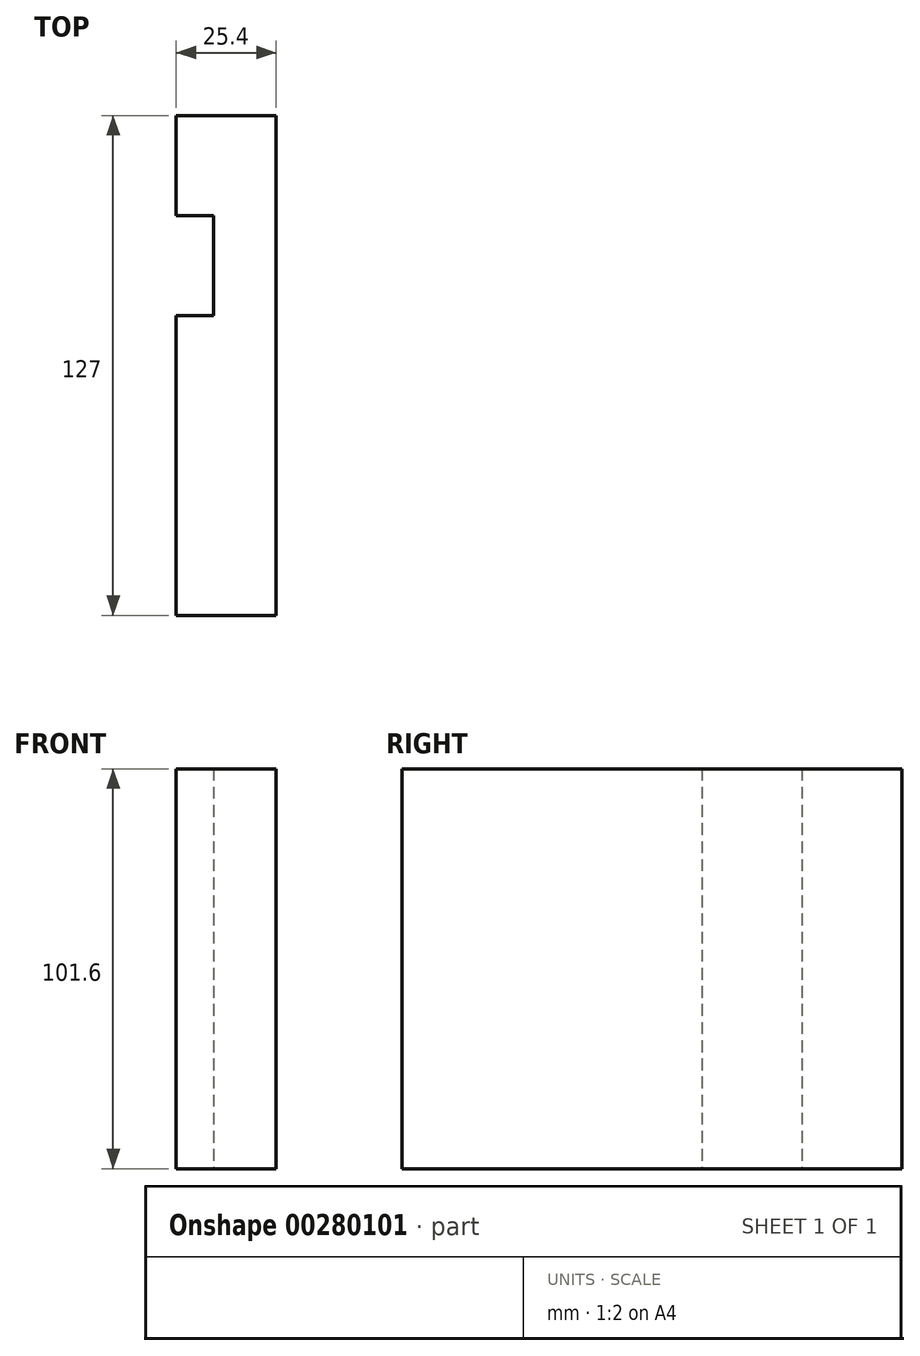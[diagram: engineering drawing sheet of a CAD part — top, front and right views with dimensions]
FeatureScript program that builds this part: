
annotation { "Feature Type Name" : "Feature", "Feature Type Description" : "" }
export const myFeature = defineFeature(function(context is Context, id is Id, definition is map)
    precondition{}
    {
        {
            var Q0;
            Q0=qCreatedBy(makeId("Top.planeOp"),FACE);
            var sketch = newSketch(context, id + "F0", { "sketchPlane" : qUnion([Q0])});
            skLineSegment(sketch, "E0", {"start": v(-9.74, 0) * mm, "end": v(-9.74, 127) * mm});
            skLineSegment(sketch, "E1", {"start": v(-9.74, 127) * mm, "end": v(-35.14, 127) * mm});
            skLineSegment(sketch, "E2", {"start": v(-35.14, 127) * mm, "end": v(-35.14, 101.6) * mm});
            skLineSegment(sketch, "E3", {"start": v(-35.14, 101.6) * mm, "end": v(-25.61, 101.6) * mm});
            skLineSegment(sketch, "E4", {"start": v(-25.61, 101.6) * mm, "end": v(-25.61, 76.2) * mm});
            skLineSegment(sketch, "E5", {"start": v(-25.61, 76.2) * mm, "end": v(-35.14, 76.2) * mm});
            skLineSegment(sketch, "E6", {"start": v(-35.14, 76.2) * mm, "end": v(-35.14, 0) * mm});
            skLineSegment(sketch, "E7", {"start": v(-9.74, 0) * mm, "end": v(-35.14, 0) * mm});
            skSolve(sketch);
        }
        {
            var Q0;
            Q0 = qSketchRegion(id + "F0", true);
            extrude(context, id + "F1", {"entities" : qUnion([Q0]), "depth" : 25.4 * mm});
        }
        {
            var Q0;
            Q0=makeQuery(id+"F1.opExtrude","CAP_FACE",FACE,{"disambiguationData":[OSD([sQuery(id+"F0.wireOp",EDGE,"E0"),sQuery(id+"F0.wireOp",EDGE,"E1"),sQuery(id+"F0.wireOp",EDGE,"E2"),sQuery(id+"F0.wireOp",EDGE,"E3"),sQuery(id+"F0.wireOp",EDGE,"E4"),sQuery(id+"F0.wireOp",EDGE,"E5"),sQuery(id+"F0.wireOp",EDGE,"E6"),sQuery(id+"F0.wireOp",EDGE,"E7")])],"isStart":false});
            var sketch = newSketch(context, id + "F2", { "sketchPlane" : qUnion([Q0])});
            skSolve(sketch);
        }
        {
            var Q0;
            Q0=makeQuery(id+"F2.imprint","IMPRINT",FACE,{"disambiguationData":[TD([[makeQuery(id+"F2.imprint","IMPRINT",EDGE,{"derivedFrom":makeQuery(id+"F1.opExtrude","CAP_EDGE",EDGE,{"disambiguationData":[OSD([sQuery(id+"F0.wireOp",EDGE,"E0")])],"isStart":false})}),1.0]])]});
            extrude(context, id + "F3", {"entities" : qUnion([Q0]), "operationType" : NewBodyOperationType.ADD, "depth" : 76.2 * mm});
        }
    });
